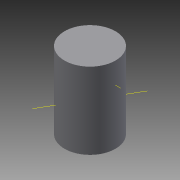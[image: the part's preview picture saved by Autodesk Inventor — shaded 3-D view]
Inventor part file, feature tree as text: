
AUTODESK INVENTOR PART (.ipt)
format: ipt  version: 2015 SP1 (Build 190203100, 203)  size: 103,936 bytes
history: native  units: mm
features: other x4, extrude x3, sketch x3
ambient origin geometry x8: Origin, YZ Plane, XZ Plane, XY Plane, X Axis, Y Axis, Z Axis, Center Point
bodies: Body1 (feature_tree)
feature tree (10):
  other  "Sólido1"
  extrude  "Extrusión1"  Depth=12.0mm
  extrude  "Extrusión2"  Depth=6.0mm TaperAngle=0.0deg
  other  "Eje de trabajo1"
  other  "Eje de trabajo2"
  extrude  "Extrusión11"  [1 undecoded]
  sketch  "Boceto1"  dims[d0=8.0mm d1=12.0mm]
  sketch  "Boceto2"  dims[d2=7.0mm d3=0.0mm d4=6.0mm d5=0.0mm]
  other  "Punto de trabajo1"
  sketch  "Boceto12"  dims[d34=5.0mm d35=0.0mm]
note: 1 required parameter value undecoded (feature->parameter linkage not recoverable at this tier; creation-order binding heuristic only, values carry confidence <= 0.55)
